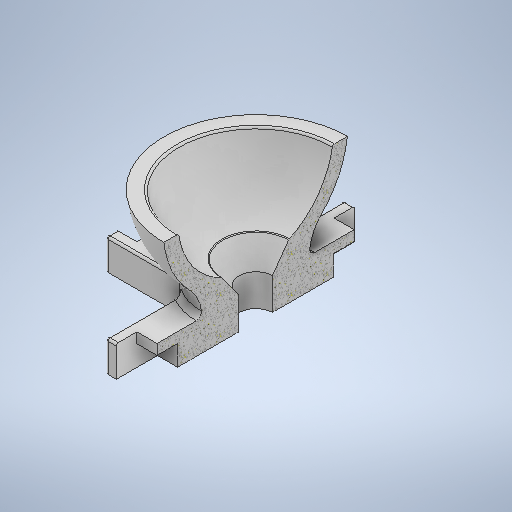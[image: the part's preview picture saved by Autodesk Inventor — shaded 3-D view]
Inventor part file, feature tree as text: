
AUTODESK INVENTOR PART (.ipt)
format: ipt  version: 2025.1 (Build 291241000, 241)  size: 772,096 bytes
history: native  units: mm
features: sketch x9, fillet x8, extrude x7, revolve x2, plane x1, chamfer x1
ambient origin geometry x8: Origin, YZ Plane, XZ Plane, XY Plane, X Axis, Y Axis, Z Axis, Center Point
bodies: Volumenkörper1 (feature_tree)
feature tree (28):
  extrude  "Extrusion1"  Depth=6.0mm TaperAngle=0.0deg
  revolve  "Umdrehung1"
  sketch  "Skizze3"  dims[d7=9.0mm d8=13.2mm]
  fillet  "Rundung1"  [1 undecoded]
  revolve  "Umdrehung2"
  extrude  "Extrusion2"  Depth=9.0mm
  plane  "Arbeitsebene1"
  extrude  "Extrusion3"  Depth=13.2mm
  chamfer  "Fasen1"  [1 undecoded]
  fillet  "Rundung2"  Radius=1.0mm
  fillet  "Rundung3"  Radius=20.0mm
  extrude  "Extrusion4"  TaperAngle=0.0deg  [1 undecoded]
  extrude  "Extrusion5"  Depth=1.0mm
  extrude  "Extrusion6"  Depth=1.0mm TaperAngle=0.0deg
  fillet  "Rundung4"  Radius=2.0mm
  fillet  "Rundung5"  Radius=0.2mm
  fillet  "Rundung6"  Radius=0.2mm
  fillet  "Rundung7"  Radius=6.0mm
  fillet  "Rundung8"  Radius=4.0mm
  extrude  "Extrusion7"  Depth=2.0mm
  sketch  "Skizze1"  dims[d0=10.5mm d1=6.0mm d2=0.0mm d3=0.0mm]
  sketch  "Skizze2"  dims[d5=9.0mm d6=9.0mm]
  sketch  "Skizze4"  dims[d9=90.0deg]
  sketch  "Skizze5"  dims[d10=7.575mm]
  sketch  "Skizze7"  dims[d11=7.575mm]
  sketch  "Skizze8"  dims[d12=7.575mm]
  sketch  "Skizze9"  dims[d13=4.0mm]
  sketch  "Skizze10"  dims[d14=90.0deg d15=0.0mm d16=1.0mm d17=20.0mm d18=0.0mm d19=0.0mm d20=3.3mm d21=20.0mm d22=0.0mm d23=1.7mm d24=2.0mm d25=45.0deg d26=0.2mm d27=0.2mm d28=6.0mm d30=4.0mm d31=0.0mm d32=2.0mm d33=4.0mm d36=4.0mm d37=2.0mm d38=0.0mm d39=2.0mm d40=4.0mm d41=0.0mm d42=0.0mm d43=2.0mm d44=4.0mm d45=4.0mm d46=2.0mm d47=0.0mm d48=4.0mm d49=2.0mm d50=0.0mm d51=2.0mm d52=4.0mm d53=0.0mm d54=3.0mm d55=0.0mm d56=0.5mm d57=0.2mm d58=0.2mm d59=0.2mm d60=0.2mm d61=11.6mm d62=1.0mm d63=30.0mm d64=0.0mm]
note: 3 required parameter values undecoded (feature->parameter linkage not recoverable at this tier; creation-order binding heuristic only, values carry confidence <= 0.55)
